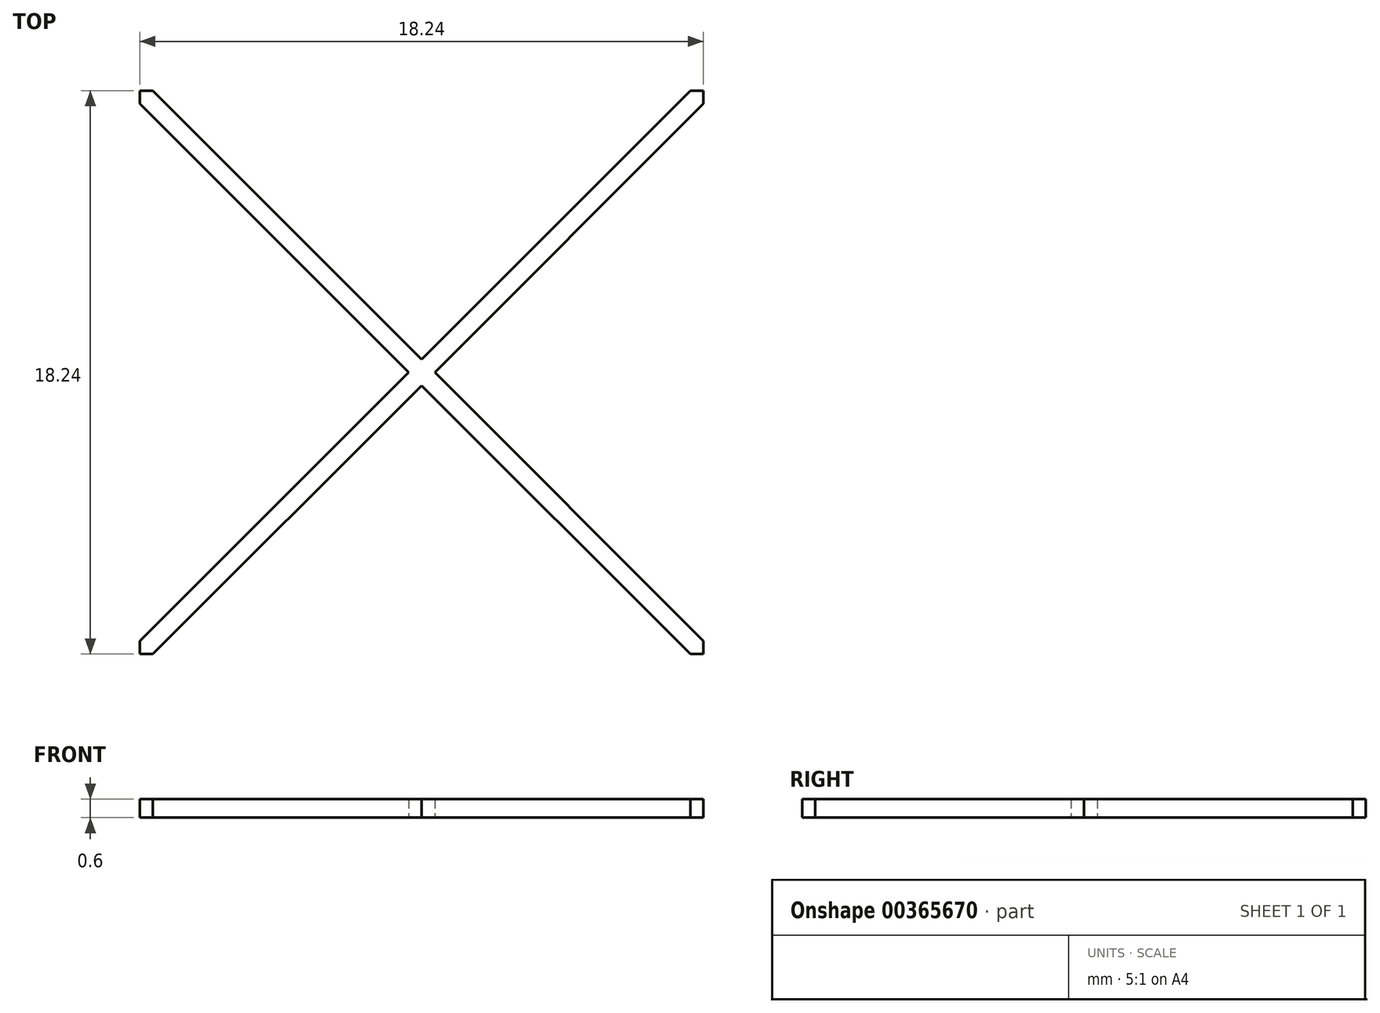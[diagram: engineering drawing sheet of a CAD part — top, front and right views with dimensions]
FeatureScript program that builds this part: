
annotation { "Feature Type Name" : "Feature", "Feature Type Description" : "" }
export const myFeature = defineFeature(function(context is Context, id is Id, definition is map)
    precondition{}
    {
        {
            var Q0;
            Q0=qCreatedBy(makeId("Top.planeOp"),FACE);
            var sketch = newSketch(context, id + "F0", { "sketchPlane" : qUnion([Q0])});
            skPoint(sketch, "E0", {"position": v(0, 0) * mm});
            skPoint(sketch, "E1", {"position": v(0, -9.12) * mm});
            skPoint(sketch, "E2", {"position": v(9.12, 0) * mm});
            skPoint(sketch, "E3", {"position": v(-9.12, 0) * mm});
            skPoint(sketch, "E4", {"position": v(0, 9.12) * mm});
            skPoint(sketch, "E5", {"position": v(-9.12, -9.12) * mm});
            skLineSegment(sketch, "E6.bottom", {"start": v(-9.12, -9.12) * mm, "end": v(9.12, -9.12) * mm});
            skLineSegment(sketch, "E6.top", {"start": v(-9.12, 9.12) * mm, "end": v(9.12, 9.12) * mm});
            skLineSegment(sketch, "E6.left", {"start": v(-9.12, -9.12) * mm, "end": v(-9.12, 9.12) * mm});
            skLineSegment(sketch, "E6.right", {"start": v(9.12, -9.12) * mm, "end": v(9.12, 9.12) * mm});
            skLineSegment(sketch, "E7", {"start": v(-9.12, -9.12) * mm, "end": v(9.12, 9.12) * mm});
            skLineSegment(sketch, "E8", {"start": v(9.12, -9.12) * mm, "end": v(-9.12, 9.12) * mm});
            skLineSegment(sketch, "E9", {"start": v(-8.7, -9.12) * mm, "end": v(9.12, 8.7) * mm});
            skLineSegment(sketch, "E10", {"start": v(-9.12, -8.7) * mm, "end": v(8.7, 9.12) * mm});
            skLineSegment(sketch, "E11", {"start": v(8.7, -9.12) * mm, "end": v(-9.12, 8.7) * mm});
            skLineSegment(sketch, "E12", {"start": v(9.12, -8.7) * mm, "end": v(-8.7, 9.12) * mm});
            skSolve(sketch);
        }
        {
            var Q0;
            {var subQ0=sQuery(id+"F0.wireOp",EDGE,"E8");var subQ5=sQuery(id+"F0.wireOp",EDGE,"E10");var subQ6=makeQuery(id+"F0.imprint","INTERSECT",VERTEX,{"derivedFrom":[subQ0,subQ5]});Q0=makeQuery(id+"F0.imprint","IMPRINT",FACE,{"disambiguationData":[TD([[makeQuery(id+"F0.imprint","IMPRINT",EDGE,{"disambiguationData":[TD([[subQ6,1.0]])],"derivedFrom":subQ5}),1.0]])]});}
            var Q1;
            {var subQ0=sQuery(id+"F0.wireOp",EDGE,"E8");var subQ5=sQuery(id+"F0.wireOp",EDGE,"E9");var subQ6=makeQuery(id+"F0.imprint","INTERSECT",VERTEX,{"derivedFrom":[subQ0,subQ5]});Q1=makeQuery(id+"F0.imprint","IMPRINT",FACE,{"disambiguationData":[TD([[makeQuery(id+"F0.imprint","IMPRINT",EDGE,{"disambiguationData":[TD([[subQ6,-1.0]])],"derivedFrom":subQ5}),-1.0]])]});}
            var Q2;
            {var subQ0=sQuery(id+"F0.wireOp",EDGE,"E8");var subQ1=sQuery(id+"F0.wireOp",EDGE,"E7");var subQ2=makeQuery(id+"F0.imprint","INTERSECT",VERTEX,{"derivedFrom":[subQ1,subQ0]});Q2=makeQuery(id+"F0.imprint","IMPRINT",FACE,{"disambiguationData":[TD([[makeQuery(id+"F0.imprint","IMPRINT",EDGE,{"disambiguationData":[TD([[subQ2,-1.0]])],"derivedFrom":subQ1}),1.0]])]});}
            var Q3;
            {var subQ0=sQuery(id+"F0.wireOp",EDGE,"E8");var subQ5=sQuery(id+"F0.wireOp",EDGE,"E9");var subQ6=makeQuery(id+"F0.imprint","INTERSECT",VERTEX,{"derivedFrom":[subQ0,subQ5]});Q3=makeQuery(id+"F0.imprint","IMPRINT",FACE,{"disambiguationData":[TD([[makeQuery(id+"F0.imprint","IMPRINT",EDGE,{"disambiguationData":[TD([[subQ6,1.0]])],"derivedFrom":subQ5}),-1.0]])]});}
            var Q4;
            {var subQ0=sQuery(id+"F0.wireOp",EDGE,"E8");var subQ5=sQuery(id+"F0.wireOp",EDGE,"E10");var subQ6=makeQuery(id+"F0.imprint","INTERSECT",VERTEX,{"derivedFrom":[subQ0,subQ5]});Q4=makeQuery(id+"F0.imprint","IMPRINT",FACE,{"disambiguationData":[TD([[makeQuery(id+"F0.imprint","IMPRINT",EDGE,{"disambiguationData":[TD([[subQ6,-1.0]])],"derivedFrom":subQ5}),1.0]])]});}
            var Q5;
            {var subQ0=sQuery(id+"F0.wireOp",EDGE,"E11");var subQ1=sQuery(id+"F0.wireOp",EDGE,"E7");var subQ2=makeQuery(id+"F0.imprint","INTERSECT",VERTEX,{"derivedFrom":[subQ1,subQ0]});Q5=makeQuery(id+"F0.imprint","IMPRINT",FACE,{"disambiguationData":[TD([[makeQuery(id+"F0.imprint","IMPRINT",EDGE,{"disambiguationData":[TD([[subQ2,-1.0]])],"derivedFrom":subQ1}),-1.0]])]});}
            var Q6;
            {var subQ0=sQuery(id+"F0.wireOp",EDGE,"E11");var subQ1=sQuery(id+"F0.wireOp",EDGE,"E7");var subQ2=makeQuery(id+"F0.imprint","INTERSECT",VERTEX,{"derivedFrom":[subQ1,subQ0]});Q6=makeQuery(id+"F0.imprint","IMPRINT",FACE,{"disambiguationData":[TD([[makeQuery(id+"F0.imprint","IMPRINT",EDGE,{"disambiguationData":[TD([[subQ2,-1.0]])],"derivedFrom":subQ1}),1.0]])]});}
            var Q7;
            {var subQ1=sQuery(id+"F0.wireOp",EDGE,"E6.bottom");var subQ3=sQuery(id+"F0.wireOp",EDGE,"E9");var subQ4=makeQuery(id+"F0.imprint","INTERSECT",VERTEX,{"derivedFrom":[subQ1,subQ3]});Q7=makeQuery(id+"F0.imprint","IMPRINT",FACE,{"disambiguationData":[TD([[makeQuery(id+"F0.imprint","IMPRINT",EDGE,{"disambiguationData":[TD([[subQ4,-1.0]])],"derivedFrom":subQ3}),1.0]])]});}
            var Q8;
            {var subQ1=sQuery(id+"F0.wireOp",EDGE,"E6.right");var subQ3=sQuery(id+"F0.wireOp",EDGE,"E9");var subQ4=makeQuery(id+"F0.imprint","INTERSECT",VERTEX,{"derivedFrom":[subQ1,subQ3]});Q8=makeQuery(id+"F0.imprint","IMPRINT",FACE,{"disambiguationData":[TD([[makeQuery(id+"F0.imprint","IMPRINT",EDGE,{"disambiguationData":[TD([[subQ4,1.0]])],"derivedFrom":subQ3}),1.0]])]});}
            var Q9;
            {var subQ1=sQuery(id+"F0.wireOp",EDGE,"E6.left");var subQ3=sQuery(id+"F0.wireOp",EDGE,"E10");var subQ4=makeQuery(id+"F0.imprint","INTERSECT",VERTEX,{"derivedFrom":[subQ1,subQ3]});Q9=makeQuery(id+"F0.imprint","IMPRINT",FACE,{"disambiguationData":[TD([[makeQuery(id+"F0.imprint","IMPRINT",EDGE,{"disambiguationData":[TD([[subQ4,-1.0]])],"derivedFrom":subQ3}),-1.0]])]});}
            var Q10;
            {var subQ0=sQuery(id+"F0.wireOp",EDGE,"E8");var subQ1=sQuery(id+"F0.wireOp",EDGE,"E7");var subQ2=makeQuery(id+"F0.imprint","INTERSECT",VERTEX,{"derivedFrom":[subQ1,subQ0]});Q10=makeQuery(id+"F0.imprint","IMPRINT",FACE,{"disambiguationData":[TD([[makeQuery(id+"F0.imprint","IMPRINT",EDGE,{"disambiguationData":[TD([[subQ2,-1.0]])],"derivedFrom":subQ1}),-1.0]])]});}
            var Q11;
            {var subQ1=sQuery(id+"F0.wireOp",EDGE,"E6.top");var subQ3=sQuery(id+"F0.wireOp",EDGE,"E10");var subQ4=makeQuery(id+"F0.imprint","INTERSECT",VERTEX,{"derivedFrom":[subQ1,subQ3]});Q11=makeQuery(id+"F0.imprint","IMPRINT",FACE,{"disambiguationData":[TD([[makeQuery(id+"F0.imprint","IMPRINT",EDGE,{"disambiguationData":[TD([[subQ4,1.0]])],"derivedFrom":subQ3}),-1.0]])]});}
            extrude(context, id + "F1", {"entities" : qUnion([Q0, Q1, Q2, Q3, Q4, Q5, Q6, Q7, Q8, Q9, Q10, Q11]), "depth" : 0.6 * mm});
        }
    });
